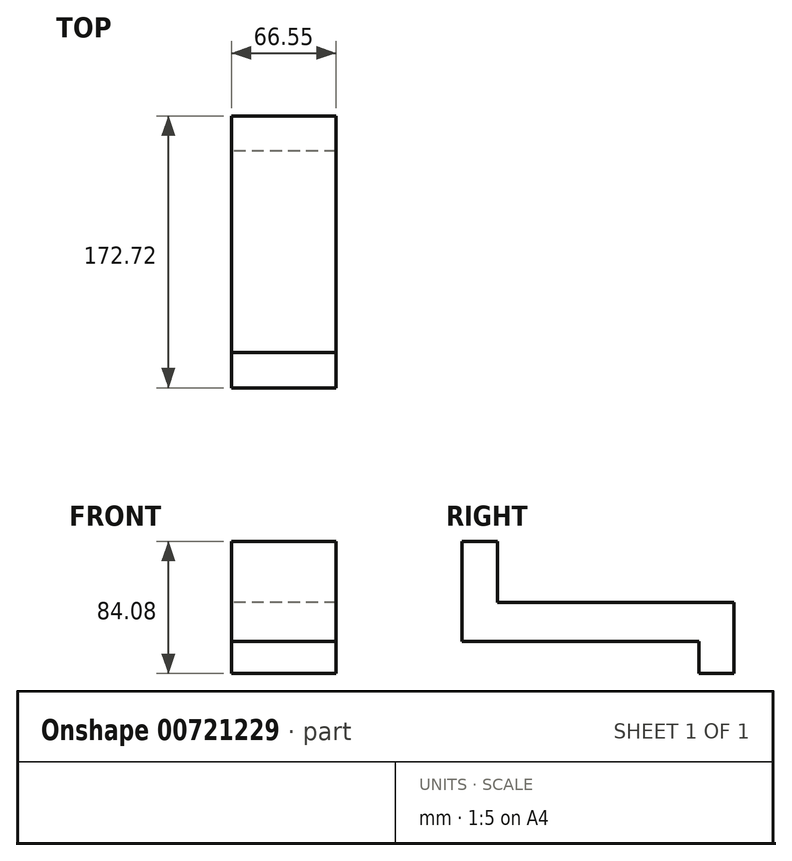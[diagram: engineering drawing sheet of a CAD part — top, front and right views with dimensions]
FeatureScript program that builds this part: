
annotation { "Feature Type Name" : "Feature", "Feature Type Description" : "" }
export const myFeature = defineFeature(function(context is Context, id is Id, definition is map)
    precondition{}
    {
        {
            var Q0;
            Q0=qCreatedBy(makeId("Right.planeOp"),FACE);
            var sketch = newSketch(context, id + "F0", { "sketchPlane" : qUnion([Q0])});
            skLineSegment(sketch, "E0.bottom", {"start": v(-86.36, -12.37) * mm, "end": v(64, -12.37) * mm});
            skLineSegment(sketch, "E0.top", {"start": v(-64, 12.37) * mm, "end": v(86.36, 12.37) * mm});
            skLineSegment(sketch, "E0.left", {"start": v(-86.36, -12.37) * mm, "end": v(-86.36, 12.37) * mm});
            skLineSegment(sketch, "E0.right", {"start": v(86.36, -12.37) * mm, "end": v(86.36, 12.37) * mm});
            skPoint(sketch, "E0.middle", {"position": v(0, 0) * mm});
            skLineSegment(sketch, "E1.bottom", {"start": v(-86.36, 51.13) * mm, "end": v(-86.36, 51.13) * mm});
            skLineSegment(sketch, "E1.top", {"start": v(-86.36, -26.39) * mm, "end": v(-86.36, -26.39) * mm});
            skLineSegment(sketch, "E1.left", {"start": v(-86.36, 51.13) * mm, "end": v(-86.36, 12.37) * mm});
            skLineSegment(sketch, "E1.right", {"start": v(-86.36, 51.13) * mm, "end": v(-86.36, -12.37) * mm});
            skPoint(sketch, "E1.middle", {"position": v(-86.36, 12.37) * mm});
            skLineSegment(sketch, "E2.bottom", {"start": v(-64, 51.13) * mm, "end": v(-86.36, 51.13) * mm});
            skLineSegment(sketch, "E2.top", {"start": v(-64, 51.13) * mm, "end": v(-86.36, 51.13) * mm});
            skLineSegment(sketch, "E2.left", {"start": v(-64, 51.13) * mm, "end": v(-64, 51.13) * mm});
            skLineSegment(sketch, "E2.right", {"start": v(-108.71, 51.13) * mm, "end": v(-108.71, 51.13) * mm});
            skPoint(sketch, "E2.middle", {"position": v(-86.36, 51.13) * mm});
            skLineSegment(sketch, "E3.bottom", {"start": v(-64, 12.37) * mm, "end": v(-64, 12.37) * mm});
            skLineSegment(sketch, "E3.top", {"start": v(-64, 89.89) * mm, "end": v(-64, 89.89) * mm});
            skLineSegment(sketch, "E3.left", {"start": v(-64, 12.37) * mm, "end": v(-64, 51.13) * mm});
            skLineSegment(sketch, "E3.right", {"start": v(-64, 12.37) * mm, "end": v(-64, 51.13) * mm});
            skPoint(sketch, "E3.middle", {"position": v(-64, 51.13) * mm});
            skLineSegment(sketch, "E4.bottom", {"start": v(86.36, -32.95) * mm, "end": v(86.36, -32.95) * mm});
            skLineSegment(sketch, "E4.top", {"start": v(86.36, 8.2) * mm, "end": v(86.36, 8.2) * mm});
            skLineSegment(sketch, "E4.left", {"start": v(86.36, -32.95) * mm, "end": v(86.36, 8.2) * mm});
            skLineSegment(sketch, "E4.right", {"start": v(86.36, -32.95) * mm, "end": v(86.36, -12.37) * mm});
            skPoint(sketch, "E4.middle", {"position": v(86.36, -12.37) * mm});
            skLineSegment(sketch, "E5", {"start": v(86.36, -32.95) * mm, "end": v(64, -32.95) * mm});
            skLineSegment(sketch, "E6", {"start": v(64, -12.37) * mm, "end": v(64, -32.95) * mm});
            skLineSegment(sketch, "E7", {"start": v(0, 1.02) * mm, "end": v(0, -21.33) * mm, "construction": true});
            skSolve(sketch);
        }
        {
            var Q0;
            Q0=makeQuery(id+"F0.imprint","IMPRINT",FACE,{"disambiguationData":[TD([[makeQuery(id+"F0.imprint","IMPRINT",EDGE,{"derivedFrom":sQuery(id+"F0.wireOp",EDGE,"E0.bottom")}),1.0]])]});
            extrude(context, id + "F1", {"entities" : qUnion([Q0]), "depth" : 66.55 * mm, "offsetDistance" : 25.4 * mm});
        }
    });
